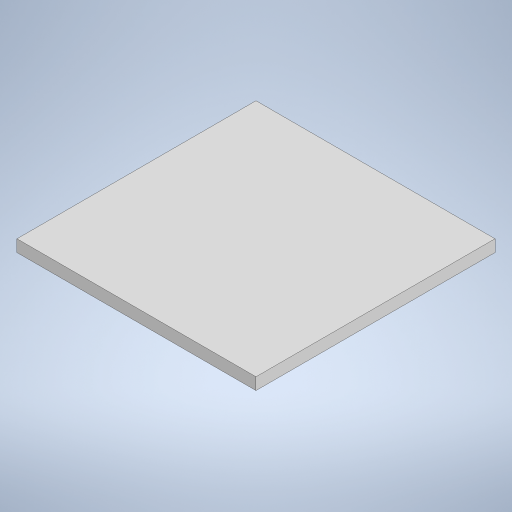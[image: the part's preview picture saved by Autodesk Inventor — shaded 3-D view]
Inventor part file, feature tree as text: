
AUTODESK INVENTOR PART (.ipt)
format: ipt  version: 2024 (Build 280153000, 153)  size: 217,600 bytes
history: native  units: in
note: dims shown in document units (in); Inventor stores cm internally (conversion verified against a paired STEP export)
features: extrude x2, sketch x2
ambient origin geometry x8: Origin, YZ Plane, XZ Plane, XY Plane, X Axis, Y Axis, Z Axis, Center Point
bodies: Body1 (feature_tree)
feature tree (4):
  extrude  "Extrusion35"  Depth=0.1181in TaperAngle=0.0deg
  extrude  "Extrusion36"  Depth=1.5748in
  sketch  "Sketch46"  dims[d158=0.315in d159=0.1181in d160=0.0in]
  sketch  "Sketch47"  dims[d161=1.5748in d162=1.5748in d163=0.0787in d164=0.0in d42=0.0197in d43=0.0344in d44=0.0197in d45=0.0344in d46=0.0in d47=0.0in d48=0.0in d49=0.0in d50=0.0in d51=0.0in d52=0.0in d53=0.0in d55=0.0197in d56=0.0344in d57=0.0197in d58=0.0344in d60=0.0197in d61=0.0344in d62=0.0197in d63=0.0344in d72=0.0197in d73=0.0344in d74=0.0197in d75=0.0344in d124=0.0197in d125=0.0344in d126=0.0197in d127=0.0344in d128=0.0344in d129=0.0197in d130=0.0344in d136=0.0197in d137=0.0344in d138=0.0197in d139=0.0344in]
